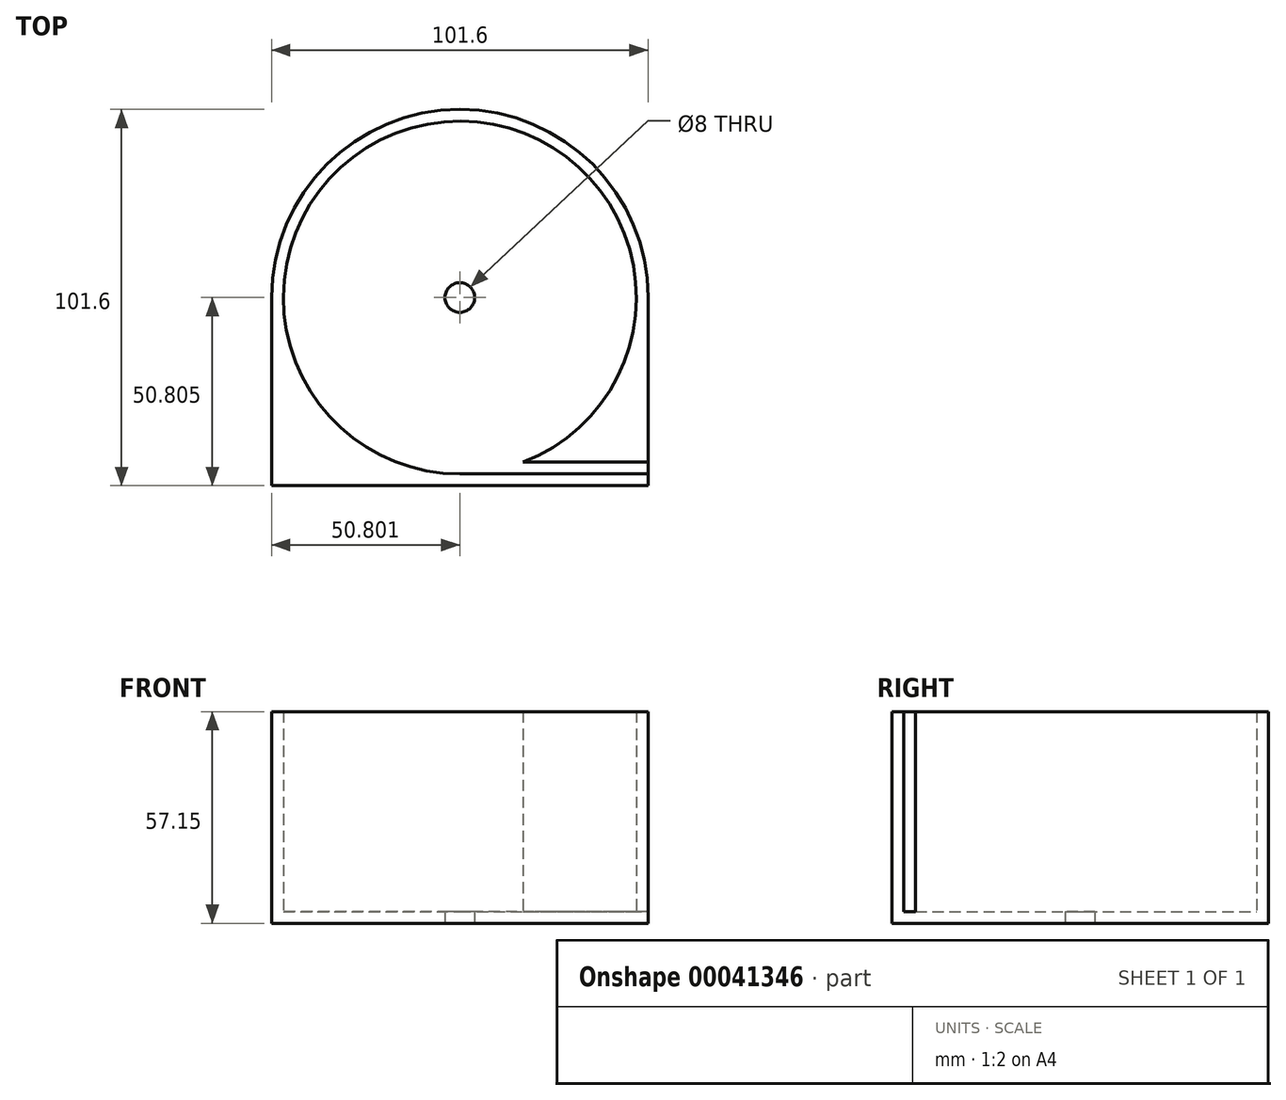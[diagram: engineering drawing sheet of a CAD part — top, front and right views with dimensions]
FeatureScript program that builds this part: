
annotation { "Feature Type Name" : "Feature", "Feature Type Description" : "" }
export const myFeature = defineFeature(function(context is Context, id is Id, definition is map)
    precondition{}
    {
        {
            var Q0;
            Q0=qCreatedBy(makeId("Top.planeOp"),FACE);
            var sketch = newSketch(context, id + "F0", { "sketchPlane" : qUnion([Q0])});
            skArc(sketch, "E0", {"start": v(-464.8, -8915.86) * mm, "mid": v(-515.6, -8865.06) * mm, "end": v(-566.4, -8915.86) * mm});
            skLineSegment(sketch, "E1.rect.top", {"start": v(-464.8, -8966.66) * mm, "end": v(-566.4, -8966.66) * mm});
            skLineSegment(sketch, "E1.rect.left", {"start": v(-464.8, -8915.86) * mm, "end": v(-464.8, -8960.3) * mm});
            skLineSegment(sketch, "E1.rect.right", {"start": v(-566.4, -8915.86) * mm, "end": v(-566.4, -8966.66) * mm});
            skPoint(sketch, "E1.rect.middle", {"position": v(-515.6, -8941.26) * mm});
            skPoint(sketch, "E2.end.orphan", {"position": v(-515.6, -8966.66) * mm});
            skCircle(sketch, "E3", {"center": v(-515.6, -8915.86) * mm, "radius": 4 * mm});
            skArc(sketch, "E4.0", {"start": v(-467.98, -8915.86) * mm, "mid": v(-515.6, -8868.23) * mm, "end": v(-563.23, -8915.86) * mm});
            skArc(sketch, "E5", {"start": v(-563.23, -8915.86) * mm, "mid": v(-549.28, -8949.53) * mm, "end": v(-515.6, -8963.48) * mm});
            skLineSegment(sketch, "E6", {"start": v(-515.6, -8963.48) * mm, "end": v(-464.8, -8963.48) * mm});
            skPoint(sketch, "E7", {"position": v(-464.8, -8960.3) * mm});
            skLineSegment(sketch, "E8", {"start": v(-464.8, -8960.3) * mm, "end": v(-498.51, -8960.3) * mm});
            skArc(sketch, "E9.trimOffspring", {"start": v(-498.51, -8960.3) * mm, "mid": v(-476.35, -8942.82) * mm, "end": v(-467.98, -8915.86) * mm});
            skLineSegment(sketch, "E10.trimOffspring", {"start": v(-464.8, -8963.48) * mm, "end": v(-464.8, -8966.66) * mm});
            skLineSegment(sketch, "E11", {"start": v(-464.8, -8960.3) * mm, "end": v(-464.8, -8963.48) * mm});
            skArc(sketch, "E12.0", {"start": v(-726.01, -8901.92) * mm, "mid": v(-773.64, -8854.3) * mm, "end": v(-821.26, -8901.92) * mm});
            skArc(sketch, "E13.trimOffspring", {"start": v(-756.54, -8946.37) * mm, "mid": v(-734.38, -8928.88) * mm, "end": v(-726.01, -8901.92) * mm});
            skLineSegment(sketch, "E14.rect.top", {"start": v(-722.84, -8952.72) * mm, "end": v(-824.44, -8952.72) * mm});
            skLineSegment(sketch, "E14.rect.left", {"start": v(-722.84, -8901.92) * mm, "end": v(-722.84, -8946.37) * mm});
            skPoint(sketch, "E14.rect.middle", {"position": v(-773.64, -8927.32) * mm});
            skLineSegment(sketch, "E15", {"start": v(-722.84, -8946.37) * mm, "end": v(-756.54, -8946.37) * mm});
            skLineSegment(sketch, "E16", {"start": v(-773.64, -8949.55) * mm, "end": v(-722.84, -8949.55) * mm});
            skLineSegment(sketch, "E14.rect.right", {"start": v(-824.44, -8901.92) * mm, "end": v(-824.44, -8952.72) * mm});
            skPoint(sketch, "E17.end.orphan", {"position": v(-773.64, -8952.72) * mm});
            skArc(sketch, "E18", {"start": v(-821.26, -8901.92) * mm, "mid": v(-807.32, -8935.6) * mm, "end": v(-773.64, -8949.55) * mm});
            skPoint(sketch, "E19", {"position": v(-722.84, -8946.37) * mm});
            skArc(sketch, "E20", {"start": v(-722.84, -8901.92) * mm, "mid": v(-773.64, -8851.12) * mm, "end": v(-824.44, -8901.92) * mm});
            skLineSegment(sketch, "E21.trimOffspring", {"start": v(-722.84, -8949.55) * mm, "end": v(-722.84, -8952.72) * mm});
            skLineSegment(sketch, "E22", {"start": v(-722.84, -8946.37) * mm, "end": v(-722.84, -8949.55) * mm});
            skCircle(sketch, "E23", {"center": v(-773.64, -8901.92) * mm, "radius": 4 * mm});
            skSolve(sketch);
        }
        {
            var Q0;
            Q0=makeQuery(id+"F0.imprint","IMPRINT",FACE,{"disambiguationData":[TD([[makeQuery(id+"F0.imprint","IMPRINT",EDGE,{"derivedFrom":sQuery(id+"F0.wireOp",EDGE,"E0")}),1.0]])]});
            extrude(context, id + "F1", {"entities" : qUnion([Q0]), "depth" : 57.15 * mm});
        }
        {
            var Q0;
            Q0=makeQuery(id+"F0.imprint","IMPRINT",FACE,{"disambiguationData":[TD([[makeQuery(id+"F0.imprint","IMPRINT",EDGE,{"derivedFrom":sQuery(id+"F0.wireOp",EDGE,"E3")}),-1.0]])]});
            extrude(context, id + "F2", {"entities" : qUnion([Q0]), "operationType" : NewBodyOperationType.ADD, "depth" : 3.17 * mm});
        }
    });
